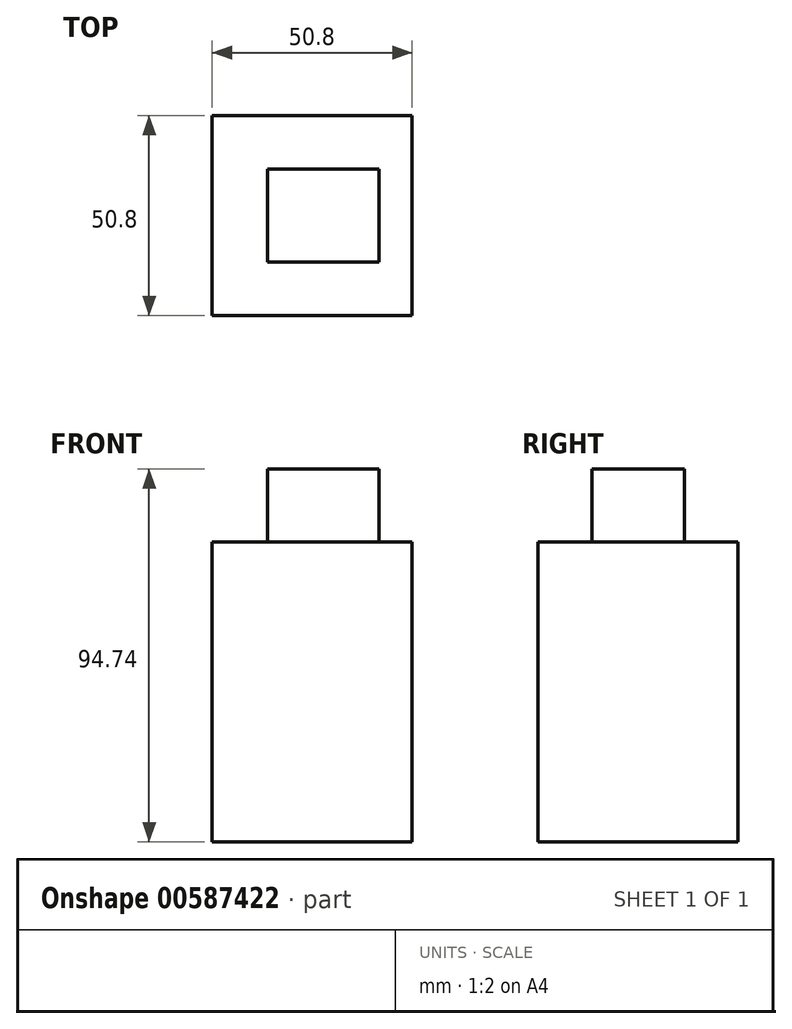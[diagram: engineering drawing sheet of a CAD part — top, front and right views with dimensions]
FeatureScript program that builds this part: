
annotation { "Feature Type Name" : "Feature", "Feature Type Description" : "" }
export const myFeature = defineFeature(function(context is Context, id is Id, definition is map)
    precondition{}
    {
        {
            var Q0;
            Q0=qCreatedBy(makeId("Top.planeOp"),FACE);
            var sketch = newSketch(context, id + "F0", { "sketchPlane" : qUnion([Q0])});
            skLineSegment(sketch, "E0.bottom", {"start": v(25.4, 25.4) * mm, "end": v(-25.4, 25.4) * mm});
            skLineSegment(sketch, "E0.top", {"start": v(25.4, -25.4) * mm, "end": v(-25.4, -25.4) * mm});
            skLineSegment(sketch, "E0.left", {"start": v(25.4, 25.4) * mm, "end": v(25.4, -25.4) * mm});
            skLineSegment(sketch, "E0.right", {"start": v(-25.4, 25.4) * mm, "end": v(-25.4, -25.4) * mm});
            skPoint(sketch, "E0.middle", {"position": v(0, 0) * mm});
            skSolve(sketch);
        }
        {
            var Q0;
            Q0 = qSketchRegion(id + "F0", true);
            extrude(context, id + "F1", {"entities" : qUnion([Q0]), "depth" : 76.2 * mm, "offsetDistance" : 25.4 * mm});
        }
        {
            var Q0;
            Q0=qCreatedBy(makeId("Top.planeOp"),FACE);
            var sketch = newSketch(context, id + "F2", { "sketchPlane" : qUnion([Q0])});
            skLineSegment(sketch, "E1.bottom", {"start": v(16.93, -11.77) * mm, "end": v(-11.28, -11.77) * mm});
            skLineSegment(sketch, "E1.top", {"start": v(16.93, 11.77) * mm, "end": v(-11.28, 11.77) * mm});
            skLineSegment(sketch, "E1.left", {"start": v(16.93, -11.77) * mm, "end": v(16.93, 11.77) * mm});
            skLineSegment(sketch, "E1.right", {"start": v(-11.28, -11.77) * mm, "end": v(-11.28, 11.77) * mm});
            skPoint(sketch, "E1.middle", {"position": v(2.82, 0) * mm});
            skSolve(sketch);
        }
        {
            var Q0;
            Q0 = qSketchRegion(id + "F2", true);
            extrude(context, id + "F3", {"entities" : qUnion([Q0]), "operationType" : NewBodyOperationType.ADD, "depth" : 94.74 * mm, "offsetDistance" : 25.4 * mm});
        }
    });
